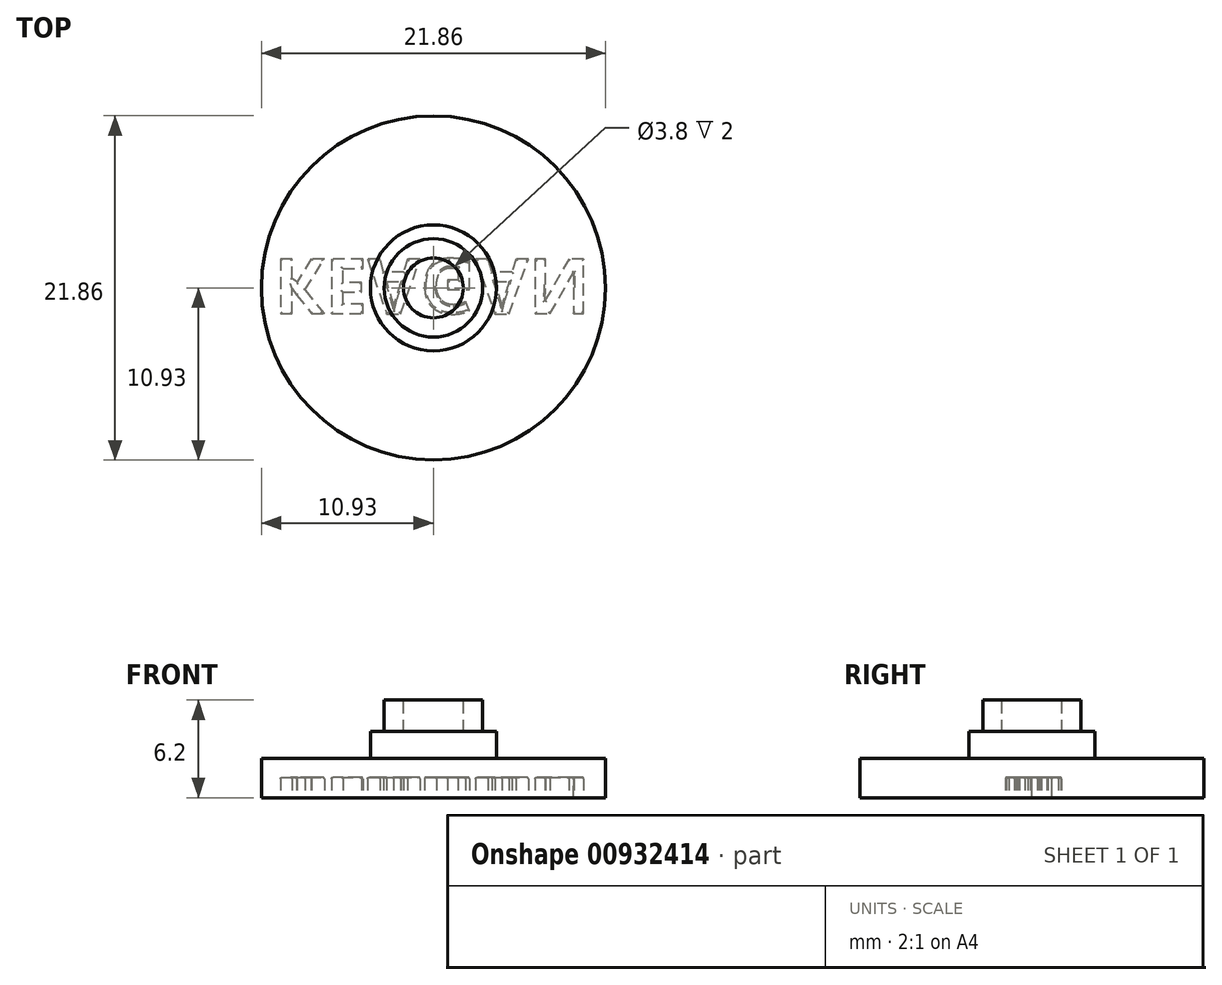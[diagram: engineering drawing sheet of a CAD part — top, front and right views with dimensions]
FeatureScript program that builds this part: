
annotation { "Feature Type Name" : "Feature", "Feature Type Description" : "" }
export const myFeature = defineFeature(function(context is Context, id is Id, definition is map)
    precondition{}
    {
        {
            var Q0;
            Q0=qCreatedBy(makeId("Top.planeOp"),FACE);
            var sketch = newSketch(context, id + "F0", { "sketchPlane" : qUnion([Q0])});
            skCircle(sketch, "E0", {"center": v(0, 0) * mm, "radius": 10.93 * mm});
            skSolve(sketch);
        }
        {
            var Q0;
            Q0=makeQuery(id+"F0.imprint","IMPRINT",FACE,{"disambiguationData":[TD([[makeQuery(id+"F0.imprint","IMPRINT",EDGE,{"derivedFrom":sQuery(id+"F0.wireOp",EDGE,"E0")}),1.0]])]});
            extrude(context, id + "F1", {"entities" : qUnion([Q0]), "depth" : 1.9 * mm, "offsetDistance" : 25 * mm});
        }
        {
            var Q0;
            Q0=makeQuery(id+"F1.opExtrude","CAP_FACE",FACE,{"disambiguationData":[OSD([sQuery(id+"F0.wireOp",EDGE,"E0")])],"isStart":false});
            var sketch = newSketch(context, id + "F2", { "sketchPlane" : qUnion([Q0])});
            skCircle(sketch, "E1", {"center": v(0, 0) * mm, "radius": 4 * mm});
            skSolve(sketch);
        }
        {
            var Q0;
            Q0 = qSketchRegion(id + "F2", true);
            extrude(context, id + "F3", {"entities" : qUnion([Q0]), "operationType" : NewBodyOperationType.ADD, "depth" : 1.7 * mm, "offsetDistance" : 25 * mm});
        }
        {
            var Q0;
            Q0=makeQuery(id+"F3.opExtrude","CAP_FACE",FACE,{"disambiguationData":[OSD([sQuery(id+"F2.wireOp",EDGE,"E1")])],"isStart":false});
            var sketch = newSketch(context, id + "F4", { "sketchPlane" : qUnion([Q0])});
            skCircle(sketch, "E2", {"center": v(0, 0) * mm, "radius": 3.12 * mm});
            skSolve(sketch);
        }
        {
            var Q0;
            Q0 = qSketchRegion(id + "F4", true);
            extrude(context, id + "F5", {"entities" : qUnion([Q0]), "operationType" : NewBodyOperationType.ADD, "depth" : 2 * mm, "offsetDistance" : 25 * mm});
        }
        {
            var Q0;
            Q0=makeQuery(id+"F5.opExtrude","CAP_FACE",FACE,{"disambiguationData":[OSD([sQuery(id+"F4.wireOp",EDGE,"E2")])],"isStart":false});
            var sketch = newSketch(context, id + "F6", { "sketchPlane" : qUnion([Q0])});
            skCircle(sketch, "E3", {"center": v(0, 0) * mm, "radius": 1.9 * mm});
            skSolve(sketch);
        }
        {
            var Q0;
            Q0 = qSketchRegion(id + "F6", true);
            extrude(context, id + "F7", {"entities" : qUnion([Q0]), "operationType" : NewBodyOperationType.REMOVE, "oppositeDirection" : true, "depth" : 2 * mm, "offsetDistance" : 25 * mm});
        }
        {
            var Q0;
            Q0=makeQuery(id+"F1.opExtrude","CAP_FACE",FACE,{"disambiguationData":[OSD([sQuery(id+"F0.wireOp",EDGE,"E0")])],"isStart":true});
            var sketch = newSketch(context, id + "F8", { "sketchPlane" : qUnion([Q0])});
            skCircle(sketch, "E4.0", {"center": v(0, 0) * mm, "radius": 10.93 * mm});
            skSolve(sketch);
        }
        {
            var Q0;
            Q0 = qSketchRegion(id + "F8", true);
            extrude(context, id + "F9", {"entities" : qUnion([Q0]), "operationType" : NewBodyOperationType.ADD, "depth" : .6 * mm, "offsetDistance" : 25 * mm});
        }
        {
            var Q0;
            Q0=makeQuery(id+"F9.opExtrude","CAP_FACE",FACE,{"disambiguationData":[OSD([sQuery(id+"F8.wireOp",EDGE,"E4.0")])],"isStart":false});
            var sketch = newSketch(context, id + "F10", { "sketchPlane" : qUnion([Q0])});
            skText(sketch, "E5", { "text": "KEAGAN", "fontName": "OpenSans-Bold.ttf"});
            const initialGuessF10  = {"E5": [-0.01015, -0.00184, 1, 0, 0.0035]};
            skSetInitialGuess(sketch, initialGuessF10);
            skSolve(sketch);
        }
        {
            var Q0;
            Q0 = qSketchRegion(id + "F10", true);
            extrude(context, id + "F11", {"entities" : qUnion([Q0]), "operationType" : NewBodyOperationType.REMOVE, "oppositeDirection" : true, "depth" : 1.3 * mm, "offsetDistance" : 25 * mm});
        }
        {
            var Q0;
            Q0=makeQuery(id+"F11.boolean.opBoolean","COPY",FACE,{"derivedFrom":makeQuery(id+"F11.opExtrude","CAP_FACE",FACE,{"disambiguationData":[OSD([sQuery(id+"F10.wireOp",EDGE,"E5.sketch_text.stroke-0"),sQuery(id+"F10.wireOp",EDGE,"E5.sketch_text.stroke-1"),sQuery(id+"F10.wireOp",EDGE,"E5.sketch_text.stroke-2"),sQuery(id+"F10.wireOp",EDGE,"E5.sketch_text.stroke-3"),sQuery(id+"F10.wireOp",EDGE,"E5.sketch_text.stroke-4"),sQuery(id+"F10.wireOp",EDGE,"E5.sketch_text.stroke-5"),sQuery(id+"F10.wireOp",EDGE,"E5.sketch_text.stroke-6"),sQuery(id+"F10.wireOp",EDGE,"E5.sketch_text.stroke-7"),sQuery(id+"F10.wireOp",EDGE,"E5.sketch_text.stroke-8"),sQuery(id+"F10.wireOp",EDGE,"E5.sketch_text.stroke-9"),sQuery(id+"F10.wireOp",EDGE,"E5.sketch_text.stroke-10"),sQuery(id+"F10.wireOp",EDGE,"E5.sketch_text.stroke-11"),sQuery(id+"F10.wireOp",EDGE,"E5.sketch_text.stroke-12")])],"isStart":false})});
            var Q1;
            Q1=makeQuery(id+"F11.boolean.opBoolean","COPY",FACE,{"derivedFrom":makeQuery(id+"F11.opExtrude","CAP_FACE",FACE,{"disambiguationData":[OSD([sQuery(id+"F10.wireOp",EDGE,"E5.sketch_text.stroke-13"),sQuery(id+"F10.wireOp",EDGE,"E5.sketch_text.stroke-14"),sQuery(id+"F10.wireOp",EDGE,"E5.sketch_text.stroke-15"),sQuery(id+"F10.wireOp",EDGE,"E5.sketch_text.stroke-16"),sQuery(id+"F10.wireOp",EDGE,"E5.sketch_text.stroke-17"),sQuery(id+"F10.wireOp",EDGE,"E5.sketch_text.stroke-18"),sQuery(id+"F10.wireOp",EDGE,"E5.sketch_text.stroke-19"),sQuery(id+"F10.wireOp",EDGE,"E5.sketch_text.stroke-20"),sQuery(id+"F10.wireOp",EDGE,"E5.sketch_text.stroke-21"),sQuery(id+"F10.wireOp",EDGE,"E5.sketch_text.stroke-22"),sQuery(id+"F10.wireOp",EDGE,"E5.sketch_text.stroke-23"),sQuery(id+"F10.wireOp",EDGE,"E5.sketch_text.stroke-24")])],"isStart":false})});
            var Q2;
            Q2=makeQuery(id+"F11.boolean.opBoolean","COPY",FACE,{"derivedFrom":makeQuery(id+"F11.opExtrude","CAP_FACE",FACE,{"disambiguationData":[OSD([sQuery(id+"F10.wireOp",EDGE,"E5.sketch_text.stroke-25"),sQuery(id+"F10.wireOp",EDGE,"E5.sketch_text.stroke-26"),sQuery(id+"F10.wireOp",EDGE,"E5.sketch_text.stroke-27"),sQuery(id+"F10.wireOp",EDGE,"E5.sketch_text.stroke-28"),sQuery(id+"F10.wireOp",EDGE,"E5.sketch_text.stroke-29"),sQuery(id+"F10.wireOp",EDGE,"E5.sketch_text.stroke-30"),sQuery(id+"F10.wireOp",EDGE,"E5.sketch_text.stroke-31"),sQuery(id+"F10.wireOp",EDGE,"E5.sketch_text.stroke-32"),sQuery(id+"F10.wireOp",EDGE,"E5.sketch_text.stroke-33"),sQuery(id+"F10.wireOp",EDGE,"E5.sketch_text.stroke-34"),sQuery(id+"F10.wireOp",EDGE,"E5.sketch_text.stroke-35"),sQuery(id+"F10.wireOp",EDGE,"E5.sketch_text.stroke-36")])],"isStart":false})});
            var Q3;
            Q3=makeQuery(id+"F11.boolean.opBoolean","COPY",FACE,{"derivedFrom":makeQuery(id+"F11.opExtrude","CAP_FACE",FACE,{"disambiguationData":[OSD([sQuery(id+"F10.wireOp",EDGE,"E5.sketch_text.stroke-37"),sQuery(id+"F10.wireOp",EDGE,"E5.sketch_text.stroke-38"),sQuery(id+"F10.wireOp",EDGE,"E5.sketch_text.stroke-39"),sQuery(id+"F10.wireOp",EDGE,"E5.sketch_text.stroke-40"),sQuery(id+"F10.wireOp",EDGE,"E5.sketch_text.stroke-41"),sQuery(id+"F10.wireOp",EDGE,"E5.sketch_text.stroke-42"),sQuery(id+"F10.wireOp",EDGE,"E5.sketch_text.stroke-43"),sQuery(id+"F10.wireOp",EDGE,"E5.sketch_text.stroke-44"),sQuery(id+"F10.wireOp",EDGE,"E5.sketch_text.stroke-45"),sQuery(id+"F10.wireOp",EDGE,"E5.sketch_text.stroke-46"),sQuery(id+"F10.wireOp",EDGE,"E5.sketch_text.stroke-47"),sQuery(id+"F10.wireOp",EDGE,"E5.sketch_text.stroke-48"),sQuery(id+"F10.wireOp",EDGE,"E5.sketch_text.stroke-49"),sQuery(id+"F10.wireOp",EDGE,"E5.sketch_text.stroke-50"),sQuery(id+"F10.wireOp",EDGE,"E5.sketch_text.stroke-51"),sQuery(id+"F10.wireOp",EDGE,"E5.sketch_text.stroke-52"),sQuery(id+"F10.wireOp",EDGE,"E5.sketch_text.stroke-53"),sQuery(id+"F10.wireOp",EDGE,"E5.sketch_text.stroke-54"),sQuery(id+"F10.wireOp",EDGE,"E5.sketch_text.stroke-55")])],"isStart":false})});
            var Q4;
            Q4=makeQuery(id+"F11.boolean.opBoolean","COPY",FACE,{"derivedFrom":makeQuery(id+"F11.opExtrude","CAP_FACE",FACE,{"disambiguationData":[OSD([sQuery(id+"F10.wireOp",EDGE,"E5.sketch_text.stroke-56"),sQuery(id+"F10.wireOp",EDGE,"E5.sketch_text.stroke-57"),sQuery(id+"F10.wireOp",EDGE,"E5.sketch_text.stroke-58"),sQuery(id+"F10.wireOp",EDGE,"E5.sketch_text.stroke-59"),sQuery(id+"F10.wireOp",EDGE,"E5.sketch_text.stroke-60"),sQuery(id+"F10.wireOp",EDGE,"E5.sketch_text.stroke-61"),sQuery(id+"F10.wireOp",EDGE,"E5.sketch_text.stroke-62"),sQuery(id+"F10.wireOp",EDGE,"E5.sketch_text.stroke-63"),sQuery(id+"F10.wireOp",EDGE,"E5.sketch_text.stroke-64"),sQuery(id+"F10.wireOp",EDGE,"E5.sketch_text.stroke-65"),sQuery(id+"F10.wireOp",EDGE,"E5.sketch_text.stroke-66"),sQuery(id+"F10.wireOp",EDGE,"E5.sketch_text.stroke-67")])],"isStart":false})});
            var Q5;
            Q5=makeQuery(id+"F11.boolean.opBoolean","COPY",FACE,{"derivedFrom":makeQuery(id+"F11.opExtrude","CAP_FACE",FACE,{"disambiguationData":[OSD([sQuery(id+"F10.wireOp",EDGE,"E5.sketch_text.stroke-68"),sQuery(id+"F10.wireOp",EDGE,"E5.sketch_text.stroke-69"),sQuery(id+"F10.wireOp",EDGE,"E5.sketch_text.stroke-70"),sQuery(id+"F10.wireOp",EDGE,"E5.sketch_text.stroke-71"),sQuery(id+"F10.wireOp",EDGE,"E5.sketch_text.stroke-72"),sQuery(id+"F10.wireOp",EDGE,"E5.sketch_text.stroke-73"),sQuery(id+"F10.wireOp",EDGE,"E5.sketch_text.stroke-74"),sQuery(id+"F10.wireOp",EDGE,"E5.sketch_text.stroke-75"),sQuery(id+"F10.wireOp",EDGE,"E5.sketch_text.stroke-76"),sQuery(id+"F10.wireOp",EDGE,"E5.sketch_text.stroke-77"),sQuery(id+"F10.wireOp",EDGE,"E5.sketch_text.stroke-78"),sQuery(id+"F10.wireOp",EDGE,"E5.sketch_text.stroke-79"),sQuery(id+"F10.wireOp",EDGE,"E5.sketch_text.stroke-80"),sQuery(id+"F10.wireOp",EDGE,"E5.sketch_text.stroke-81")])],"isStart":false})});
            fillet(context, id + "F12", {"entities" : qUnion([Q0, Q1, Q2, Q3, Q4, Q5]), "radius" : 0.1 * mm, "tangentPropagation" : true, "allowEdgeOverflow" : false});
        }
    });
